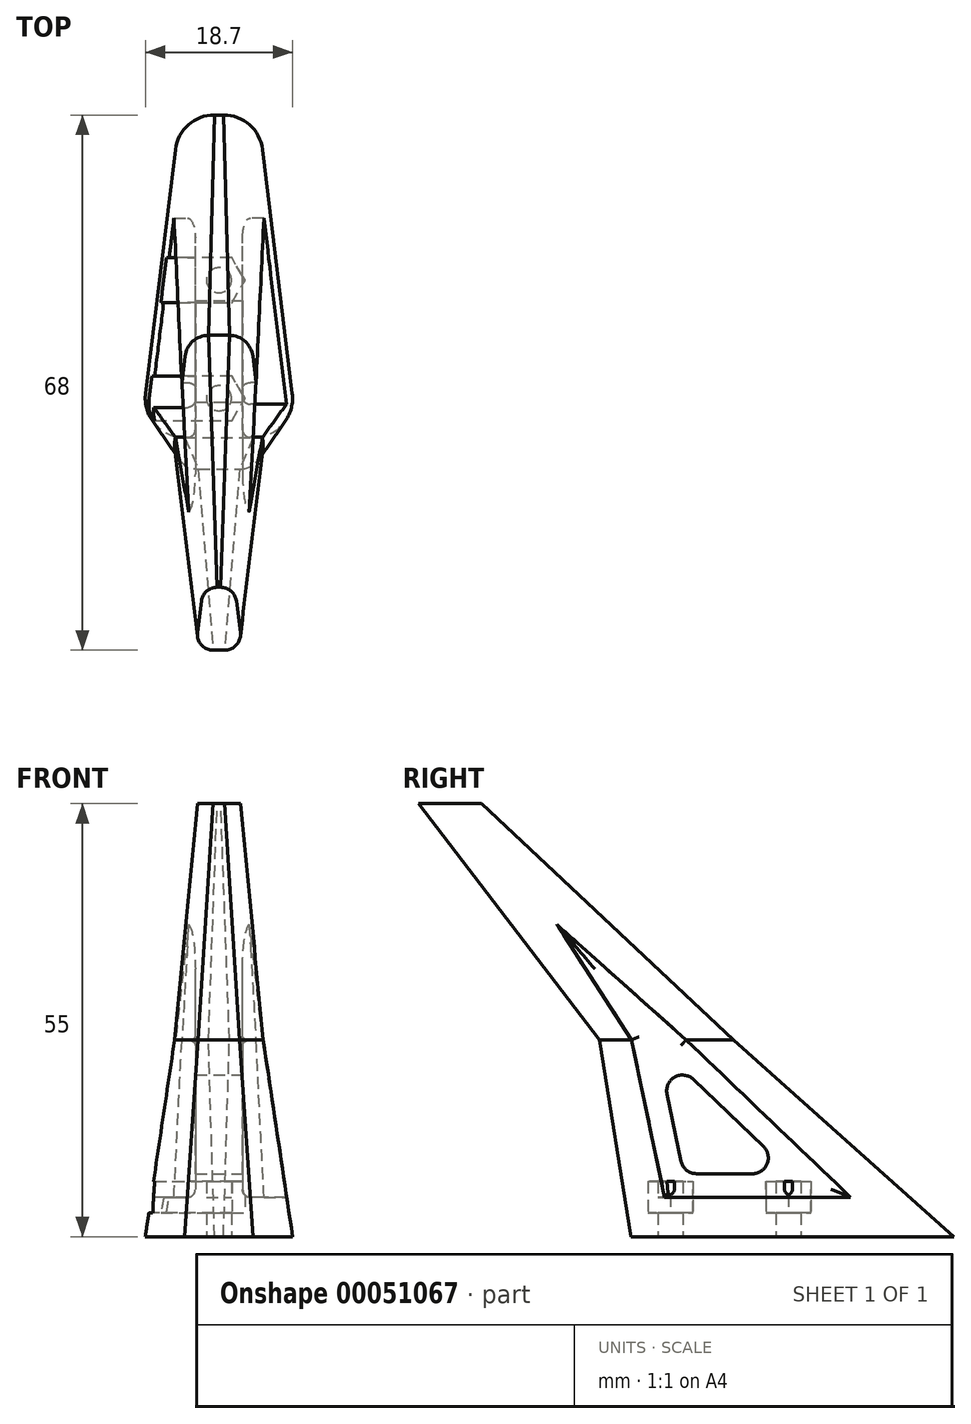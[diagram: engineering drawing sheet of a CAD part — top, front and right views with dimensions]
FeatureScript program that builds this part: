
annotation { "Feature Type Name" : "Feature", "Feature Type Description" : "" }
export const myFeature = defineFeature(function(context is Context, id is Id, definition is map)
    precondition{}
    {
        {
            var Q0;
            Q0=qCreatedBy(makeId("Top.planeOp"),FACE);
            var sketch = newSketch(context, id + "F0", { "sketchPlane" : qUnion([Q0])});
            skLineSegment(sketch, "E0", {"start": v(0, 0) * mm, "end": v(0, 7.5) * mm, "construction": true});
            skLineSegment(sketch, "E1", {"start": v(0, 0) * mm, "end": v(0, -7.5) * mm, "construction": true});
            skLineSegment(sketch, "E2", {"start": v(0, 0) * mm, "end": v(0, -16) * mm, "construction": true});
            skLineSegment(sketch, "E3", {"start": v(0, 0) * mm, "end": v(0, 25) * mm, "construction": true});
            skLineSegment(sketch, "E4", {"start": v(0, 25) * mm, "end": v(-0.57, 25) * mm});
            skLineSegment(sketch, "E5", {"start": v(-5.54, 20.6) * mm, "end": v(-9.32, -10.4) * mm});
            skLineSegment(sketch, "E6", {"start": v(-4.35, -16) * mm, "end": v(0, -16) * mm});
            skPoint(sketch, "E7.visualSharp", {"position": v(-5, 25) * mm});
            skArc(sketch, "E7.filletArc", {"start": v(-0.57, 25) * mm, "mid": v(-3.89, 23.74) * mm, "end": v(-5.54, 20.6) * mm});
            skPoint(sketch, "E8.visualSharp", {"position": v(-10, -16) * mm});
            skArc(sketch, "E8.filletArc", {"start": v(-9.32, -10.4) * mm, "mid": v(-8.1, -14.31) * mm, "end": v(-4.35, -16) * mm});
            skLineSegment(sketch, "E9.MirrorCS", {"start": v(0, 25) * mm, "end": v(0.57, 25) * mm});
            skArc(sketch, "E10.MirrorCS", {"start": v(0.57, 25) * mm, "mid": v(3.89, 23.74) * mm, "end": v(5.54, 20.6) * mm});
            skLineSegment(sketch, "E11.MirrorCS", {"start": v(5.54, 20.6) * mm, "end": v(9.32, -10.4) * mm});
            skArc(sketch, "E12.MirrorCS", {"start": v(9.32, -10.4) * mm, "mid": v(8.1, -14.31) * mm, "end": v(4.35, -16) * mm});
            skLineSegment(sketch, "E13.MirrorCS", {"start": v(4.35, -16) * mm, "end": v(0, -16) * mm});
            skSolve(sketch);
        }
        {
            var Q0;
            Q0=makeQuery(id+"F0.imprint","IMPRINT",FACE,{"disambiguationData":[TD([[makeQuery(id+"F0.imprint","IMPRINT",EDGE,{"derivedFrom":sQuery(id+"F0.wireOp",EDGE,"E4")}),1.0]])]});
            cPlane(context, id + "F1", {"entities" : qUnion([Q0]), "cplaneType" : CPlaneType.OFFSET, "offset" : 25 * mm, "width" : 150 * mm, "height" : 150 * mm});
        }
        {
            var Q0;
            Q0=qCreatedBy(id+"F1.planeOp",FACE);
            var sketch = newSketch(context, id + "F2", { "sketchPlane" : qUnion([Q0])});
            skLineSegment(sketch, "E14", {"start": v(0, 0) * mm, "end": v(0, -15) * mm, "construction": true});
            skLineSegment(sketch, "E15", {"start": v(0, -15) * mm, "end": v(0, -3) * mm, "construction": true});
            skLineSegment(sketch, "E16", {"start": v(0, -15) * mm, "end": v(0, -20) * mm, "construction": true});
            skLineSegment(sketch, "E17", {"start": v(0, -3) * mm, "end": v(-1.33, -3) * mm});
            skLineSegment(sketch, "E18", {"start": v(-4.31, -5.65) * mm, "end": v(-5.6, -16.65) * mm});
            skLineSegment(sketch, "E19", {"start": v(-2.63, -20) * mm, "end": v(0, -20) * mm});
            skPoint(sketch, "E20.visualSharp", {"position": v(-4, -3) * mm});
            skArc(sketch, "E20.filletArc", {"start": v(-1.33, -3) * mm, "mid": v(-3.33, -3.76) * mm, "end": v(-4.31, -5.65) * mm});
            skPoint(sketch, "E21.visualSharp", {"position": v(-6, -20) * mm});
            skArc(sketch, "E21.filletArc", {"start": v(-5.6, -16.65) * mm, "mid": v(-4.87, -19) * mm, "end": v(-2.63, -20) * mm});
            skLineSegment(sketch, "E22.MirrorCS", {"start": v(0, -3) * mm, "end": v(1.33, -3) * mm});
            skArc(sketch, "E23.MirrorCS", {"start": v(1.33, -3) * mm, "mid": v(3.33, -3.76) * mm, "end": v(4.31, -5.65) * mm});
            skLineSegment(sketch, "E24.MirrorCS", {"start": v(4.31, -5.65) * mm, "end": v(5.6, -16.65) * mm});
            skArc(sketch, "E25.MirrorCS", {"start": v(5.6, -16.65) * mm, "mid": v(4.87, -19) * mm, "end": v(2.63, -20) * mm});
            skLineSegment(sketch, "E26.MirrorCS", {"start": v(2.63, -20) * mm, "end": v(0, -20) * mm});
            skSolve(sketch);
        }
        {
            var Q0;
            Q0=makeQuery(id+"F0.imprint","IMPRINT",FACE,{"disambiguationData":[TD([[makeQuery(id+"F0.imprint","IMPRINT",EDGE,{"derivedFrom":sQuery(id+"F0.wireOp",EDGE,"E4")}),1.0]])]});
            var Q1;
            Q1=makeQuery(id+"F2.imprint","IMPRINT",FACE,{"disambiguationData":[TD([[makeQuery(id+"F2.imprint","IMPRINT",EDGE,{"derivedFrom":sQuery(id+"F2.wireOp",EDGE,"E17")}),1.0]])]});
            loft(context, id + "F3", {"sheetProfilesArray" : [{ "sheetProfileEntities" : qUnion([Q0]) }, { "sheetProfileEntities" : qUnion([Q1]) }]});
        }
        {
            var Q0;
            Q0=makeQuery(id+"F3.opLoft","CAP_FACE",FACE,{"disambiguationData":[OSD([makeQuery(id+"F2.imprint","IMPRINT",FACE,{"disambiguationData":[TD([[makeQuery(id+"F2.imprint","IMPRINT",EDGE,{"derivedFrom":sQuery(id+"F2.wireOp",EDGE,"E17")}),1.0]])]})])],"isStart":true});
            cPlane(context, id + "F4", {"entities" : qUnion([Q0]), "cplaneType" : CPlaneType.OFFSET, "offset" : 30 * mm, "width" : 150 * mm, "height" : 150 * mm});
        }
        {
            var Q0;
            Q0=qCreatedBy(id+"F4.planeOp",FACE);
            var sketch = newSketch(context, id + "F5", { "sketchPlane" : qUnion([Q0])});
            skLineSegment(sketch, "E27", {"start": v(0, 0) * mm, "end": v(0, -40) * mm, "construction": true});
            skLineSegment(sketch, "E28", {"start": v(0, -40) * mm, "end": v(0, -35) * mm, "construction": true});
            skLineSegment(sketch, "E29", {"start": v(0, -40) * mm, "end": v(0, -43) * mm, "construction": true});
            skLineSegment(sketch, "E30", {"start": v(0, -35) * mm, "end": v(-0.23, -35) * mm});
            skLineSegment(sketch, "E31", {"start": v(-2.22, -36.75) * mm, "end": v(-2.72, -40.75) * mm});
            skLineSegment(sketch, "E32", {"start": v(-0.73, -43) * mm, "end": v(0, -43) * mm});
            skPoint(sketch, "E33.visualSharp", {"position": v(-2, -35) * mm});
            skArc(sketch, "E33.filletArc", {"start": v(-0.23, -35) * mm, "mid": v(-1.56, -35.5) * mm, "end": v(-2.22, -36.75) * mm});
            skPoint(sketch, "E34.visualSharp", {"position": v(-3, -43) * mm});
            skArc(sketch, "E34.filletArc", {"start": v(-2.72, -40.75) * mm, "mid": v(-2.23, -42.32) * mm, "end": v(-0.73, -43) * mm});
            skLineSegment(sketch, "E35.MirrorCS", {"start": v(0, -35) * mm, "end": v(0.23, -35) * mm});
            skArc(sketch, "E36.MirrorCS", {"start": v(0.23, -35) * mm, "mid": v(1.56, -35.5) * mm, "end": v(2.22, -36.75) * mm});
            skLineSegment(sketch, "E37.MirrorCS", {"start": v(2.22, -36.75) * mm, "end": v(2.72, -40.75) * mm});
            skArc(sketch, "E38.MirrorCS", {"start": v(2.72, -40.75) * mm, "mid": v(2.23, -42.32) * mm, "end": v(0.73, -43) * mm});
            skLineSegment(sketch, "E39.MirrorCS", {"start": v(0.73, -43) * mm, "end": v(0, -43) * mm});
            skSolve(sketch);
        }
        {
            var Q1;
            Q1 = qSketchRegion(id + "F2", true);
            var Q2;
            Q2 = qSketchRegion(id + "F5", true);
            loft(context, id + "F6", {"operationType" : NewBodyOperationType.ADD, "sheetProfilesArray" : [{ "sheetProfileEntities" : qUnion([Q1]) }, { "sheetProfileEntities" : qUnion([Q2]) }]});
        }
        {
            var Q0;
            Q0=qCreatedBy(makeId("Right.planeOp"),FACE);
            var sketch = newSketch(context, id + "F7", { "sketchPlane" : qUnion([Q0])});
            skLineSegment(sketch, "E40", {"start": v(-3, 25) * mm, "end": v(-9, 25) * mm, "construction": true});
            skLineSegment(sketch, "E41", {"start": v(-20, 25) * mm, "end": v(-15.95, 25) * mm, "construction": true});
            skLineSegment(sketch, "E42", {"start": v(-15.95, 25) * mm, "end": v(-9, 25) * mm, "construction": true});
            skLineSegment(sketch, "E43", {"start": v(-10.94, 0) * mm, "end": v(-11.74, 5) * mm, "construction": true});
            skLineSegment(sketch, "E44", {"start": v(17.5, 0) * mm, "end": v(11.9, 5) * mm, "construction": true});
            skLineSegment(sketch, "E45", {"start": v(-11.74, 5) * mm, "end": v(11.9, 5) * mm});
            skLineSegment(sketch, "E46", {"start": v(-16, 0) * mm, "end": v(-16.85, 5.3) * mm, "construction": true});
            skLineSegment(sketch, "E47", {"start": v(25, 0) * mm, "end": v(14.62, 9.27) * mm, "construction": true});
            skLineSegment(sketch, "E48", {"start": v(-15.95, 25) * mm, "end": v(-11.74, 5) * mm});
            skLineSegment(sketch, "E49", {"start": v(-9, 25) * mm, "end": v(11.9, 5) * mm});
            skLineSegment(sketch, "E50", {"start": v(-3, 25) * mm, "end": v(-0.44, 22.72) * mm, "construction": true});
            skLineSegment(sketch, "E51", {"start": v(-20, 25) * mm, "end": v(-19.63, 22.7) * mm, "construction": true});
            skLineSegment(sketch, "E52", {"start": v(-35, 55) * mm, "end": v(-43, 55) * mm, "construction": true});
            skLineSegment(sketch, "E53", {"start": v(-39, 55) * mm, "end": v(-12.48, 25) * mm, "construction": true});
            skLineSegment(sketch, "E54", {"start": v(-9, 25) * mm, "end": v(-25.49, 39.72) * mm});
            skLineSegment(sketch, "E55", {"start": v(-15.95, 25) * mm, "end": v(-25.49, 39.72) * mm});
            skSolve(sketch);
        }
        {
            var Q0;
            Q0 = qSketchRegion(id + "F7", true);
            extrude(context, id + "F8", {"entities" : qUnion([Q0]), "operationType" : NewBodyOperationType.REMOVE, "oppositeDirection" : true, "depth" : 25 * mm, "hasSecondDirection" : true, "secondDirectionOppositeDirection" : true, "secondDirectionDepth" : 3 * mm});
        }
        {
            var Q0;
            Q0 = qSketchRegion(id + "F7", true);
            extrude(context, id + "F9", {"entities" : qUnion([Q0]), "operationType" : NewBodyOperationType.REMOVE, "depth" : 25 * mm, "hasSecondDirection" : true, "secondDirectionOppositeDirection" : false, "secondDirectionDepth" : 3 * mm});
        }
        {
            var Q0;
            Q0=makeQuery(id+"F8.boolean.opBoolean","COPY",EDGE,{"derivedFrom":makeQuery(id+"F8.opExtrude","CAP_EDGE",EDGE,{"disambiguationData":[OSD([sQuery(id+"F7.wireOp",EDGE,"E54")])],"isStart":true})});
            var Q1;
            Q1=makeQuery(id+"F8.boolean.opBoolean","COPY",EDGE,{"derivedFrom":makeQuery(id+"F8.opExtrude","CAP_EDGE",EDGE,{"disambiguationData":[OSD([sQuery(id+"F7.wireOp",EDGE,"E49")])],"isStart":true})});
            var Q2;
            Q2=makeQuery(id+"F8.boolean.opBoolean","COPY",EDGE,{"derivedFrom":makeQuery(id+"F8.opExtrude","CAP_EDGE",EDGE,{"disambiguationData":[OSD([sQuery(id+"F7.wireOp",EDGE,"E55")])],"isStart":true})});
            var Q3;
            Q3=makeQuery(id+"F8.boolean.opBoolean","COPY",EDGE,{"derivedFrom":makeQuery(id+"F8.opExtrude","CAP_EDGE",EDGE,{"disambiguationData":[OSD([sQuery(id+"F7.wireOp",EDGE,"E48")])],"isStart":true})});
            var Q4;
            Q4=makeQuery(id+"F8.boolean.opBoolean","COPY",EDGE,{"derivedFrom":makeQuery(id+"F8.opExtrude","CAP_EDGE",EDGE,{"disambiguationData":[OSD([sQuery(id+"F7.wireOp",EDGE,"E45")])],"isStart":true})});
            var Q5;
            Q5=makeQuery(id+"F9.boolean.opBoolean","COPY",EDGE,{"derivedFrom":makeQuery(id+"F9.opExtrude","CAP_EDGE",EDGE,{"disambiguationData":[OSD([sQuery(id+"F7.wireOp",EDGE,"E48")])],"isStart":true})});
            var Q6;
            Q6=makeQuery(id+"F9.boolean.opBoolean","COPY",EDGE,{"derivedFrom":makeQuery(id+"F9.opExtrude","CAP_EDGE",EDGE,{"disambiguationData":[OSD([sQuery(id+"F7.wireOp",EDGE,"E45")])],"isStart":true})});
            var Q7;
            Q7=makeQuery(id+"F9.boolean.opBoolean","COPY",EDGE,{"derivedFrom":makeQuery(id+"F9.opExtrude","CAP_EDGE",EDGE,{"disambiguationData":[OSD([sQuery(id+"F7.wireOp",EDGE,"E55")])],"isStart":true})});
            var Q8;
            Q8=makeQuery(id+"F9.boolean.opBoolean","COPY",EDGE,{"derivedFrom":makeQuery(id+"F9.opExtrude","CAP_EDGE",EDGE,{"disambiguationData":[OSD([sQuery(id+"F7.wireOp",EDGE,"E54")])],"isStart":true})});
            var Q9;
            Q9=makeQuery(id+"F9.boolean.opBoolean","COPY",EDGE,{"derivedFrom":makeQuery(id+"F9.opExtrude","CAP_EDGE",EDGE,{"disambiguationData":[OSD([sQuery(id+"F7.wireOp",EDGE,"E49")])],"isStart":true})});
            fillet(context, id + "F10", {"entities" : qUnion([Q0, Q1, Q2, Q3, Q4, Q5, Q6, Q7, Q8, Q9]), "radius" : 1 * mm, "tangentPropagation" : true, "allowEdgeOverflow" : false});
        }
        {
            var Q0;
            Q0=makeQuery(id+"F3.opLoft","CAP_FACE",FACE,{"disambiguationData":[OSD([makeQuery(id+"F0.imprint","IMPRINT",FACE,{"disambiguationData":[TD([[makeQuery(id+"F0.imprint","IMPRINT",EDGE,{"derivedFrom":sQuery(id+"F0.wireOp",EDGE,"E4")}),1.0]])]})])],"isStart":true});
            var sketch = newSketch(context, id + "F11", { "sketchPlane" : qUnion([Q0])});
            skCircle(sketch, "E56", {"center": v(0, 11) * mm, "radius": 1.6 * mm});
            skCircle(sketch, "E57", {"center": v(0, -4) * mm, "radius": 1.6 * mm});
            skLineSegment(sketch, "E58", {"start": v(0, 16) * mm, "end": v(0, 11) * mm, "construction": true});
            skLineSegment(sketch, "E59", {"start": v(0, 11) * mm, "end": v(0, -4) * mm, "construction": true});
            skSolve(sketch);
        }
        {
            var Q0;
            Q0=makeQuery(id+"F11.imprint","IMPRINT",FACE,{"disambiguationData":[TD([[makeQuery(id+"F11.imprint","IMPRINT",EDGE,{"derivedFrom":sQuery(id+"F11.wireOp",EDGE,"E56")}),1.0]])]});
            var Q1;
            Q1=makeQuery(id+"F11.imprint","IMPRINT",FACE,{"disambiguationData":[TD([[makeQuery(id+"F11.imprint","IMPRINT",EDGE,{"derivedFrom":sQuery(id+"F11.wireOp",EDGE,"E57")}),1.0]])]});
            var Q2;
            Q2=makeQuery(id+"F8.boolean.opBoolean","COPY",FACE,{"derivedFrom":makeQuery(id+"F8.opExtrude","SWEPT_FACE",FACE,{"disambiguationData":[OSD([sQuery(id+"F7.wireOp",EDGE,"E45")])]})});
            extrude(context, id + "F12", {"entities" : qUnion([Q0, Q1]), "operationType" : NewBodyOperationType.REMOVE, "endBound" : BoundingType.UP_TO_SURFACE, "oppositeDirection" : true, "endBoundEntityFace" : qUnion([Q2]), "depth" : 25 * mm});
        }
        {
            var Q0;
            Q0=makeQuery(id+"F9.boolean.opBoolean","COPY",FACE,{"derivedFrom":makeQuery(id+"F9.opExtrude","CAP_FACE",FACE,{"disambiguationData":[OSD([sQuery(id+"F7.wireOp",EDGE,"E45"),sQuery(id+"F7.wireOp",EDGE,"E48"),sQuery(id+"F7.wireOp",EDGE,"E49"),sQuery(id+"F7.wireOp",EDGE,"E54"),sQuery(id+"F7.wireOp",EDGE,"E55")])],"isStart":true})});
            var sketch = newSketch(context, id + "F13", { "sketchPlane" : qUnion([Q0])});
            skLineSegment(sketch, "E60.0", {"start": v(0.82, 11.44) * mm, "end": v(-8.1, 19.97) * mm});
            skLineSegment(sketch, "E60.1", {"start": v(-7.68, 8) * mm, "end": v(-0.56, 8) * mm});
            skLineSegment(sketch, "E60.2", {"start": v(-11.43, 18.12) * mm, "end": v(-9.64, 9.59) * mm});
            skPoint(sketch, "E61.visualSharp", {"position": v(4.42, 8) * mm});
            skArc(sketch, "E61.filletArc", {"start": v(-0.56, 8) * mm, "mid": v(1.3, 9.25) * mm, "end": v(0.82, 11.44) * mm});
            skPoint(sketch, "E62.visualSharp", {"position": v(-9.3, 8) * mm});
            skArc(sketch, "E62.filletArc", {"start": v(-9.64, 9.59) * mm, "mid": v(-8.94, 8.45) * mm, "end": v(-7.68, 8) * mm});
            skPoint(sketch, "E63.visualSharp", {"position": v(-12.77, 24.45) * mm});
            skArc(sketch, "E63.filletArc", {"start": v(-8.1, 19.97) * mm, "mid": v(-10.45, 20.28) * mm, "end": v(-11.43, 18.12) * mm});
            skSolve(sketch);
        }
        {
            var Q0;
            Q0=makeQuery(id+"F13.imprint","IMPRINT",FACE,{"disambiguationData":[TD([[makeQuery(id+"F13.imprint","IMPRINT",EDGE,{"derivedFrom":sQuery(id+"F13.wireOp",EDGE,"E60.0")}),1.0]])]});
            var Q1;
            Q1 = qConstructionFilter(qBodyType(qCreatedBy(id + "F13" ,EDGE), BodyType.WIRE), ConstructionObject.NO);
            extrude(context, id + "F14", {"entities" : qUnion([Q0]), "operationType" : NewBodyOperationType.REMOVE, "surfaceEntities" : qUnion([Q1]), "oppositeDirection" : true, "depth" : 25 * mm});
        }
        {
            var Q0;
            Q0=makeQuery(id+"F3.opLoft","CAP_FACE",FACE,{"disambiguationData":[OSD([makeQuery(id+"F0.imprint","IMPRINT",FACE,{"disambiguationData":[TD([[makeQuery(id+"F0.imprint","IMPRINT",EDGE,{"derivedFrom":sQuery(id+"F0.wireOp",EDGE,"E4")}),1.0]])]})])],"isStart":true});
            var sketch = newSketch(context, id + "F15", { "sketchPlane" : qUnion([Q0])});
            skCircle(sketch, "E64.cCircle", {"center": v(0, 11) * mm, "radius": 2.85 * mm, "construction": true});
            skLineSegment(sketch, "E64.0", {"start": v(1.65, 8.15) * mm, "end": v(-1.65, 8.15) * mm});
            skLineSegment(sketch, "E64.1", {"start": v(-1.65, 8.15) * mm, "end": v(-3.3, 11) * mm});
            skLineSegment(sketch, "E64.2", {"start": v(-3.3, 11) * mm, "end": v(-1.65, 13.85) * mm});
            skLineSegment(sketch, "E64.3", {"start": v(-1.65, 13.85) * mm, "end": v(1.65, 13.85) * mm});
            skLineSegment(sketch, "E64.4", {"start": v(1.65, 13.85) * mm, "end": v(3.3, 11) * mm});
            skLineSegment(sketch, "E64.5", {"start": v(3.3, 11) * mm, "end": v(1.65, 8.15) * mm});
            skPoint(sketch, "E64.0.midPoint", {"position": v(0, 8.15) * mm});
            skCircle(sketch, "E65.cCircle", {"center": v(0, -4) * mm, "radius": 2.85 * mm, "construction": true});
            skLineSegment(sketch, "E65.0", {"start": v(1.65, -6.85) * mm, "end": v(-1.65, -6.85) * mm});
            skLineSegment(sketch, "E65.1", {"start": v(-1.65, -6.85) * mm, "end": v(-3.3, -4) * mm});
            skLineSegment(sketch, "E65.2", {"start": v(-3.3, -4) * mm, "end": v(-1.65, -1.15) * mm});
            skLineSegment(sketch, "E65.3", {"start": v(-1.65, -1.15) * mm, "end": v(1.65, -1.15) * mm});
            skLineSegment(sketch, "E65.4", {"start": v(1.65, -1.15) * mm, "end": v(3.3, -4) * mm});
            skLineSegment(sketch, "E65.5", {"start": v(3.3, -4) * mm, "end": v(1.65, -6.85) * mm});
            skPoint(sketch, "E65.0.midPoint", {"position": v(0, -6.85) * mm});
            skLineSegment(sketch, "E66", {"start": v(-1.65, 13.85) * mm, "end": v(-13.11, 13.85) * mm});
            skLineSegment(sketch, "E67", {"start": v(-13.11, 13.85) * mm, "end": v(-13.11, 8.15) * mm});
            skLineSegment(sketch, "E68", {"start": v(-13.11, 8.15) * mm, "end": v(-1.65, 8.15) * mm});
            skLineSegment(sketch, "E69", {"start": v(-1.65, -1.15) * mm, "end": v(-13.93, -1.15) * mm});
            skLineSegment(sketch, "E70", {"start": v(-13.93, -1.15) * mm, "end": v(-13.93, -6.85) * mm});
            skLineSegment(sketch, "E71", {"start": v(-13.93, -6.85) * mm, "end": v(-1.65, -6.85) * mm});
            skSolve(sketch);
        }
        {
            var Q0;
            Q0=makeQuery(id+"F15.imprint","IMPRINT",FACE,{"disambiguationData":[TD([[makeQuery(id+"F15.imprint","IMPRINT",EDGE,{"derivedFrom":sQuery(id+"F15.wireOp",EDGE,"E64.0")}),-1.0]])]});
            var Q1;
            {var subQ1=sQuery(id+"F15.wireOp",EDGE,"E64.1");Q1=makeQuery(id+"F15.imprint","IMPRINT",FACE,{"disambiguationData":[TD([[makeQuery(id+"F15.imprint","IMPRINT",EDGE,{"derivedFrom":subQ1}),1.0]])]});}
            var Q2;
            {var subQ7=sQuery(id+"F15.wireOp",EDGE,"E67");Q2=makeQuery(id+"F15.imprint","IMPRINT",FACE,{"disambiguationData":[TD([[makeQuery(id+"F15.imprint","IMPRINT",EDGE,{"derivedFrom":subQ7}),1.0]])]});}
            var Q3;
            Q3=makeQuery(id+"F15.imprint","IMPRINT",FACE,{"disambiguationData":[TD([[makeQuery(id+"F15.imprint","IMPRINT",EDGE,{"derivedFrom":sQuery(id+"F15.wireOp",EDGE,"E65.0")}),-1.0]])]});
            var Q4;
            {var subQ0=sQuery(id+"F15.wireOp",EDGE,"E70");Q4=makeQuery(id+"F15.imprint","IMPRINT",FACE,{"disambiguationData":[TD([[makeQuery(id+"F15.imprint","IMPRINT",EDGE,{"derivedFrom":subQ0}),1.0]])]});}
            var Q5;
            Q5=makeQuery(id+"F15.imprint","IMPRINT",FACE,{"disambiguationData":[TD([[makeQuery(id+"F15.imprint","IMPRINT",EDGE,{"derivedFrom":makeQuery(id+"F12.boolean.opBoolean","COPY",EDGE,{"derivedFrom":makeQuery(id+"F12.opExtrude","CAP_EDGE",EDGE,{"disambiguationData":[OSD([sQuery(id+"F11.wireOp",EDGE,"E56")])],"isStart":true})})}),1.0]])]});
            var Q6;
            Q6=makeQuery(id+"F15.imprint","IMPRINT",FACE,{"disambiguationData":[TD([[makeQuery(id+"F15.imprint","IMPRINT",EDGE,{"derivedFrom":makeQuery(id+"F12.boolean.opBoolean","COPY",EDGE,{"derivedFrom":makeQuery(id+"F12.opExtrude","CAP_EDGE",EDGE,{"disambiguationData":[OSD([sQuery(id+"F11.wireOp",EDGE,"E57")])],"isStart":true})})}),1.0]])]});
            var Q7;
            {var subQ1=sQuery(id+"F15.wireOp",EDGE,"E65.1");Q7=makeQuery(id+"F15.imprint","IMPRINT",FACE,{"disambiguationData":[TD([[makeQuery(id+"F15.imprint","IMPRINT",EDGE,{"derivedFrom":subQ1}),1.0]])]});}
            extrude(context, id + "F16", {"entities" : qUnion([Q0, Q1, Q2, Q3, Q4, Q5, Q6, Q7]), "operationType" : NewBodyOperationType.REMOVE, "oppositeDirection" : true, "depth" : 7 * mm, "hasSecondDirection" : true, "secondDirectionOppositeDirection" : true, "secondDirectionDepth" : 3 * mm});
        }
    });
